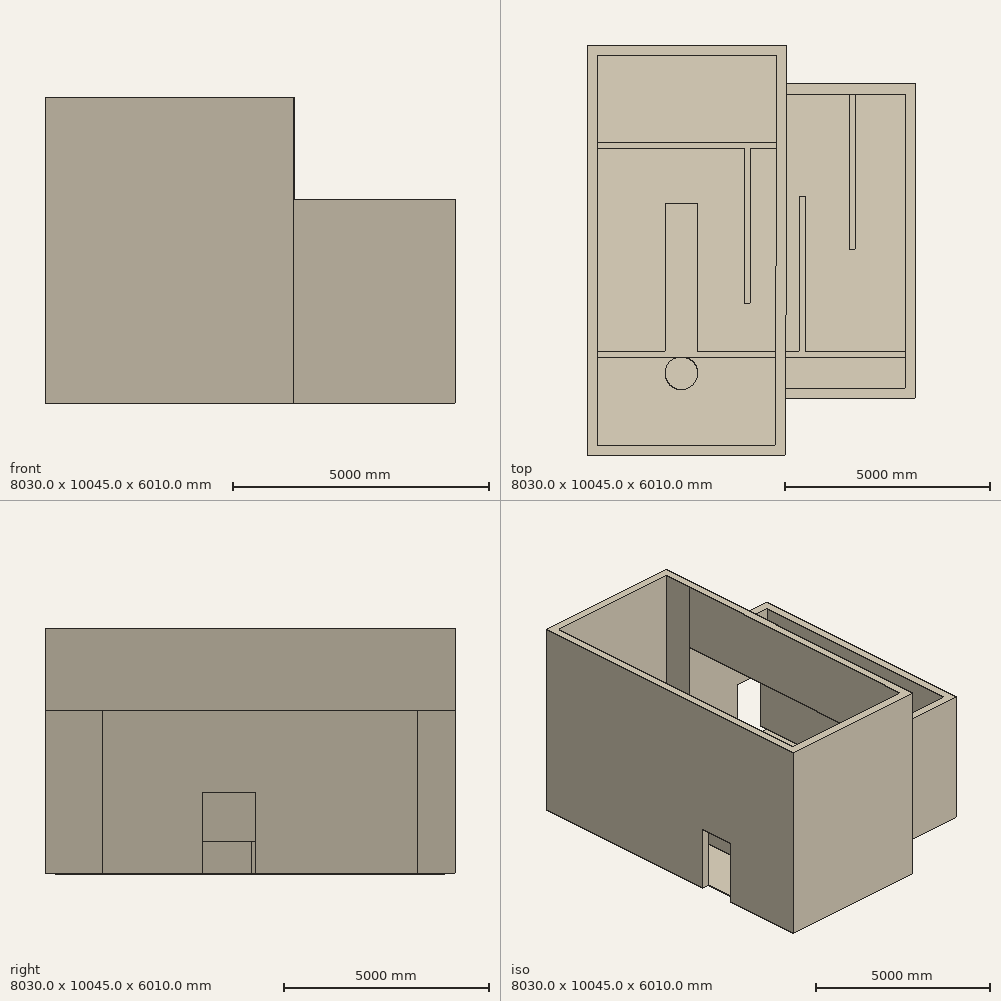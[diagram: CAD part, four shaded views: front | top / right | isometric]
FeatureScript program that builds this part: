
annotation { "Feature Type Name" : "Feature", "Feature Type Description" : "" }
export const myFeature = defineFeature(function(context is Context, id is Id, definition is map)
    precondition{}
    {
        {
            var Q0;
            Q0=qCreatedBy(makeId("Top.planeOp"),FACE);
            var sketch = newSketch(context, id + "F0", { "sketchPlane" : qUnion([Q0])});
            skLineSegment(sketch, "E0", {"start": v(0, 9545) * mm, "end": v(0, 0) * mm});
            skLineSegment(sketch, "E1", {"start": v(0, 0) * mm, "end": v(4350, 0) * mm});
            skLineSegment(sketch, "E2", {"start": v(4350, 0) * mm, "end": v(4350, 1400) * mm});
            skLineSegment(sketch, "E3", {"start": v(4350, 1400) * mm, "end": v(7530, 1400) * mm});
            skLineSegment(sketch, "E4", {"start": v(7530, 1400) * mm, "end": v(7530, 8605) * mm});
            skLineSegment(sketch, "E5", {"start": v(7530, 8605) * mm, "end": v(4380, 8605) * mm});
            skLineSegment(sketch, "E6", {"start": v(4380, 8605) * mm, "end": v(4380, 9545) * mm});
            skLineSegment(sketch, "E7", {"start": v(4380, 9545) * mm, "end": v(0, 9545) * mm});
            skSolve(sketch);
        }
        {
            var Q0;
            Q0 = qSketchRegion(id + "F0", true);
            extrude(context, id + "F1", {"entities" : qUnion([Q0]), "depth" : 10 * mm});
        }
        {
            var Q0;
            Q0=makeQuery(id+"F1.opExtrude","CAP_FACE",FACE,{"disambiguationData":[OSD([sQuery(id+"F0.wireOp",EDGE,"E0"),sQuery(id+"F0.wireOp",EDGE,"E1"),sQuery(id+"F0.wireOp",EDGE,"E2"),sQuery(id+"F0.wireOp",EDGE,"E3"),sQuery(id+"F0.wireOp",EDGE,"E4"),sQuery(id+"F0.wireOp",EDGE,"E5"),sQuery(id+"F0.wireOp",EDGE,"E6"),sQuery(id+"F0.wireOp",EDGE,"E7")])],"isStart":false});
            var sketch = newSketch(context, id + "F2", { "sketchPlane" : qUnion([Q0])});
            skLineSegment(sketch, "E8", {"start": v(4380, 8605) * mm, "end": v(4380, 7275) * mm, "construction": true});
            skLineSegment(sketch, "E9", {"start": v(4380, 7275) * mm, "end": v(3740, 7275) * mm, "construction": true});
            skLineSegment(sketch, "E10", {"start": v(7530, 2300) * mm, "end": v(2440, 2300) * mm, "construction": true});
            skLineSegment(sketch, "E11.top", {"start": v(3600, 3475) * mm, "end": v(3740, 3475) * mm});
            skLineSegment(sketch, "E11.left", {"start": v(3600, 7275) * mm, "end": v(3600, 3475) * mm});
            skLineSegment(sketch, "E11.right", {"start": v(3740, 7275) * mm, "end": v(3740, 3475) * mm});
            skLineSegment(sketch, "E12.top", {"start": v(2440, 5930) * mm, "end": v(1660, 5930) * mm});
            skLineSegment(sketch, "E12.left", {"start": v(2440, 2300) * mm, "end": v(2440, 5930) * mm});
            skLineSegment(sketch, "E12.right", {"start": v(1660, 2300) * mm, "end": v(1660, 5930) * mm});
            skLineSegment(sketch, "E13.bottom", {"start": v(5080, 2300) * mm, "end": v(4940, 2300) * mm});
            skLineSegment(sketch, "E13.top", {"start": v(5080, 6100) * mm, "end": v(4940, 6100) * mm});
            skLineSegment(sketch, "E13.left", {"start": v(5080, 2300) * mm, "end": v(5080, 6100) * mm});
            skLineSegment(sketch, "E13.right", {"start": v(4940, 2300) * mm, "end": v(4940, 6100) * mm});
            skLineSegment(sketch, "E14.bottom", {"start": v(6170, 8605) * mm, "end": v(6310, 8605) * mm});
            skLineSegment(sketch, "E14.top", {"start": v(6170, 4805) * mm, "end": v(6310, 4805) * mm});
            skLineSegment(sketch, "E14.left", {"start": v(6310, 8605) * mm, "end": v(6310, 4805) * mm});
            skLineSegment(sketch, "E14.right", {"start": v(6170, 8605) * mm, "end": v(6170, 4805) * mm});
            skLineSegment(sketch, "E15", {"start": v(0, 7275) * mm, "end": v(3600, 7275) * mm});
            skLineSegment(sketch, "E16", {"start": v(4520, 7275) * mm, "end": v(4520, 8605) * mm});
            skLineSegment(sketch, "E17", {"start": v(4520, 8605) * mm, "end": v(4380, 8605) * mm});
            skLineSegment(sketch, "E18", {"start": v(4380, 7415) * mm, "end": v(0, 7415) * mm});
            skLineSegment(sketch, "E19", {"start": v(0, 7415) * mm, "end": v(0, 7275) * mm});
            skLineSegment(sketch, "E20", {"start": v(4380, 8605) * mm, "end": v(4380, 7415) * mm});
            skLineSegment(sketch, "E21.trimOffspring", {"start": v(3600, 7275) * mm, "end": v(0, 7275) * mm, "construction": true});
            skLineSegment(sketch, "E22.trimOffspring", {"start": v(3740, 7275) * mm, "end": v(4520, 7275) * mm});
            skLineSegment(sketch, "E23.trimOffspring", {"start": v(1660, 2300) * mm, "end": v(0, 2300) * mm, "construction": true});
            skLineSegment(sketch, "E24.bottom", {"start": v(0, 2300) * mm, "end": v(1660, 2300) * mm});
            skLineSegment(sketch, "E24.top", {"start": v(0, 2160) * mm, "end": v(7530, 2160) * mm});
            skLineSegment(sketch, "E24.left", {"start": v(0, 2300) * mm, "end": v(0, 2160) * mm});
            skLineSegment(sketch, "E24.right", {"start": v(7530, 2300) * mm, "end": v(7530, 2160) * mm});
            skLineSegment(sketch, "E25.trimOffspring", {"start": v(2440, 2300) * mm, "end": v(7530, 2300) * mm});
            skSolve(sketch);
        }
        {
            var Q0;
            {var subQ0=sQuery(id+"F0.wireOp",EDGE,"E7");var subQ1=sQuery(id+"F0.wireOp",EDGE,"E6");var subQ2=sQuery(id+"F0.wireOp",EDGE,"E5");var subQ3=sQuery(id+"F0.wireOp",EDGE,"E0");Q0=makeQuery(id+"F4.boolean.opBoolean","SPLIT",FACE,{"disambiguationData":[TD([makeQuery(id+"F1.opExtrude","SWEPT_FACE",FACE,{"disambiguationData":[OSD([subQ1])]})])],"derivedFrom":makeQuery(id+"F1.opExtrude","CAP_FACE",FACE,{"disambiguationData":[OSD([subQ3,sQuery(id+"F0.wireOp",EDGE,"E1"),sQuery(id+"F0.wireOp",EDGE,"E2"),sQuery(id+"F0.wireOp",EDGE,"E3"),sQuery(id+"F0.wireOp",EDGE,"E4"),subQ2,subQ1,subQ0])],"isStart":false})});}
            var sketch = newSketch(context, id + "F3", { "sketchPlane" : qUnion([Q0])});
            skLineSegment(sketch, "E26", {"start": v(0, 9545) * mm, "end": v(0, 0) * mm});
            skLineSegment(sketch, "E27", {"start": v(0, 0) * mm, "end": v(4350, 0) * mm});
            skLineSegment(sketch, "E28", {"start": v(4350, 0) * mm, "end": v(4350, 1400) * mm});
            skLineSegment(sketch, "E29", {"start": v(4350, 1400) * mm, "end": v(7530, 1400) * mm});
            skLineSegment(sketch, "E30", {"start": v(7530, 1400) * mm, "end": v(7530, 8605) * mm});
            skLineSegment(sketch, "E31", {"start": v(7530, 8605) * mm, "end": v(4380, 8605) * mm});
            skLineSegment(sketch, "E32", {"start": v(4380, 8605) * mm, "end": v(4380, 9545) * mm});
            skLineSegment(sketch, "E33", {"start": v(4380, 9545) * mm, "end": v(0, 9545) * mm});
            skLineSegment(sketch, "E34.0", {"start": v(4630, 8855) * mm, "end": v(4630, 9795) * mm});
            skLineSegment(sketch, "E34.1", {"start": v(7780, 8855) * mm, "end": v(4630, 8855) * mm});
            skLineSegment(sketch, "E34.2", {"start": v(4630, 9795) * mm, "end": v(-250, 9795) * mm});
            skLineSegment(sketch, "E34.3", {"start": v(7780, 1150) * mm, "end": v(7780, 8855) * mm});
            skLineSegment(sketch, "E34.4", {"start": v(-250, 9795) * mm, "end": v(-250, -250) * mm});
            skLineSegment(sketch, "E34.5", {"start": v(-250, -250) * mm, "end": v(4600, -250) * mm});
            skLineSegment(sketch, "E34.6", {"start": v(4600, -250) * mm, "end": v(4600, 1150) * mm});
            skLineSegment(sketch, "E34.7", {"start": v(4600, 1150) * mm, "end": v(7780, 1150) * mm});
            skSolve(sketch);
        }
        {
            var Q0;
            Q0 = qSketchRegion(id + "F2", true);
            extrude(context, id + "F4", {"entities" : qUnion([Q0]), "operationType" : NewBodyOperationType.ADD, "depth" : 800 * mm});
        }
        {
            var Q0;
            Q0 = qSketchRegion(id + "F3", true);
            extrude(context, id + "F5", {"entities" : qUnion([Q0]), "depth" : 4000 * mm});
        }
        {
            var Q0;
            Q0=makeQuery(id+"F5.opExtrude","SWEPT_FACE",FACE,{"disambiguationData":[OSD([sQuery(id+"F3.wireOp",EDGE,"E26")])]});
            var sketch = newSketch(context, id + "F6", { "sketchPlane" : qUnion([Q0])});
            skLineSegment(sketch, "E35", {"start": v(2300, 10) * mm, "end": v(2300, 1950) * mm});
            skLineSegment(sketch, "E36", {"start": v(2300, 1950) * mm, "end": v(3440, 1950) * mm});
            skLineSegment(sketch, "E37", {"start": v(3440, 1950) * mm, "end": v(3440, 0) * mm});
            skLineSegment(sketch, "E38", {"start": v(3440, 0) * mm, "end": v(2300, 10) * mm});
            skSolve(sketch);
        }
        {
            var Q0;
            Q0 = qSketchRegion(id + "F6", true);
            extrude(context, id + "F7", {"entities" : qUnion([Q0]), "operationType" : NewBodyOperationType.REMOVE, "endBound" : BoundingType.THROUGH_ALL, "oppositeDirection" : true, "depth" : 25 * mm});
        }
        {
            var Q0;
            Q0=makeQuery(id+"F5.opExtrude","SWEPT_FACE",FACE,{"disambiguationData":[OSD([sQuery(id+"F3.wireOp",EDGE,"E31")])]});
            var sketch = newSketch(context, id + "F8", { "sketchPlane" : qUnion([Q0])});
            skLineSegment(sketch, "E39", {"start": v(7530, 10) * mm, "end": v(7530, 1960) * mm});
            skLineSegment(sketch, "E40", {"start": v(7530, 1960) * mm, "end": v(6310, 1960) * mm});
            skLineSegment(sketch, "E41", {"start": v(6310, 1960) * mm, "end": v(6310, 0) * mm});
            skLineSegment(sketch, "E42", {"start": v(6310, 0) * mm, "end": v(7530, 10) * mm});
            skSolve(sketch);
        }
        {
            var Q0;
            Q0 = qSketchRegion(id + "F8", true);
            extrude(context, id + "F9", {"entities" : qUnion([Q0]), "operationType" : NewBodyOperationType.REMOVE, "endBound" : BoundingType.THROUGH_ALL, "oppositeDirection" : true, "depth" : 25 * mm});
        }
        {
            var Q0;
            Q0=makeQuery(id+"F9.boolean.opBoolean","MERGE",FACE,{"derivedFrom":[makeQuery(id+"F5.opExtrude","SWEPT_FACE",FACE,{"disambiguationData":[OSD([sQuery(id+"F3.wireOp",EDGE,"E30")])]}),makeQuery(id+"F9.opExtrude","SWEPT_FACE",FACE,{"disambiguationData":[OSD([sQuery(id+"F8.wireOp",EDGE,"E39")])]})]});
            var sketch = newSketch(context, id + "F10", { "sketchPlane" : qUnion([Q0])});
            skLineSegment(sketch, "E43", {"start": v(-4905, 10) * mm, "end": v(-3585, 10) * mm});
            skLineSegment(sketch, "E44", {"start": v(-3585, 10) * mm, "end": v(-3585, 2010) * mm});
            skLineSegment(sketch, "E45", {"start": v(-3585, 2010) * mm, "end": v(-4905, 2010) * mm});
            skLineSegment(sketch, "E46", {"start": v(-4905, 2010) * mm, "end": v(-4905, 10) * mm});
            skSolve(sketch);
        }
        {
            var Q0;
            Q0 = qSketchRegion(id + "F10", true);
            extrude(context, id + "F11", {"entities" : qUnion([Q0]), "operationType" : NewBodyOperationType.REMOVE, "endBound" : BoundingType.THROUGH_ALL, "oppositeDirection" : true, "depth" : 25 * mm});
        }
        {
            var Q0;
            Q0=makeQuery(id+"F5.opExtrude","CAP_FACE",FACE,{"disambiguationData":[OSD([sQuery(id+"F3.wireOp",EDGE,"E26"),sQuery(id+"F3.wireOp",EDGE,"E27"),sQuery(id+"F3.wireOp",EDGE,"E28"),sQuery(id+"F3.wireOp",EDGE,"E29"),sQuery(id+"F3.wireOp",EDGE,"E30"),sQuery(id+"F3.wireOp",EDGE,"E31"),sQuery(id+"F3.wireOp",EDGE,"E32"),sQuery(id+"F3.wireOp",EDGE,"E33"),sQuery(id+"F3.wireOp",EDGE,"E34.0"),sQuery(id+"F3.wireOp",EDGE,"E34.1"),sQuery(id+"F3.wireOp",EDGE,"E34.2"),sQuery(id+"F3.wireOp",EDGE,"E34.3"),sQuery(id+"F3.wireOp",EDGE,"E34.4"),sQuery(id+"F3.wireOp",EDGE,"E34.5"),sQuery(id+"F3.wireOp",EDGE,"E34.6"),sQuery(id+"F3.wireOp",EDGE,"E34.7")])],"isStart":false});
            var sketch = newSketch(context, id + "F12", { "sketchPlane" : qUnion([Q0])});
            skLineSegment(sketch, "E47", {"start": v(4380, 8605) * mm, "end": v(4380, 9545) * mm});
            skLineSegment(sketch, "E48", {"start": v(4380, 9545) * mm, "end": v(0, 9545) * mm});
            skLineSegment(sketch, "E49", {"start": v(0, 9545) * mm, "end": v(0, 0) * mm});
            skLineSegment(sketch, "E50", {"start": v(0, 0) * mm, "end": v(4350, 0) * mm});
            skLineSegment(sketch, "E51", {"start": v(4350, 0) * mm, "end": v(4380, 8605) * mm});
            skLineSegment(sketch, "E52", {"start": v(-250, 9795) * mm, "end": v(4630, 9795) * mm});
            skLineSegment(sketch, "E53", {"start": v(4630, 9795) * mm, "end": v(4600, -250) * mm});
            skLineSegment(sketch, "E54", {"start": v(4600, -250) * mm, "end": v(-250, -250) * mm});
            skLineSegment(sketch, "E55", {"start": v(-250, -250) * mm, "end": v(-250, 9795) * mm});
            skSolve(sketch);
        }
        {
            var Q0;
            Q0 = qSketchRegion(id + "F12", true);
            extrude(context, id + "F13", {"entities" : qUnion([Q0]), "operationType" : NewBodyOperationType.ADD, "depth" : 2000 * mm});
        }
        {
            var Q0;
            {var subQ0=sQuery(id+"F0.wireOp",EDGE,"E2");var subQ1=sQuery(id+"F0.wireOp",EDGE,"E1");var subQ2=sQuery(id+"F0.wireOp",EDGE,"E3");var subQ3=sQuery(id+"F0.wireOp",EDGE,"E0");var subQ4=sQuery(id+"F0.wireOp",EDGE,"E4");Q0=makeQuery(id+"F4.boolean.opBoolean","SPLIT",FACE,{"disambiguationData":[TD([makeQuery(id+"F1.opExtrude","SWEPT_FACE",FACE,{"disambiguationData":[OSD([subQ1])]})])],"derivedFrom":makeQuery(id+"F1.opExtrude","CAP_FACE",FACE,{"disambiguationData":[OSD([subQ3,subQ1,subQ0,subQ2,subQ4,sQuery(id+"F0.wireOp",EDGE,"E5"),sQuery(id+"F0.wireOp",EDGE,"E6"),sQuery(id+"F0.wireOp",EDGE,"E7")])],"isStart":false})});}
            var sketch = newSketch(context, id + "F14", { "sketchPlane" : qUnion([Q0])});
            skCircle(sketch, "E56", {"center": v(2050, 1760) * mm, "radius": 400 * mm});
            skLineSegment(sketch, "E57", {"start": v(2050, 1760) * mm, "end": v(2050, 5930) * mm, "construction": true});
            skSolve(sketch);
        }
        {
            var Q0;
            Q0 = qSketchRegion(id + "F14", true);
            extrude(context, id + "F15", {"entities" : qUnion([Q0]), "operationType" : NewBodyOperationType.REMOVE, "oppositeDirection" : true, "depth" : 1 * mm});
        }
    });
